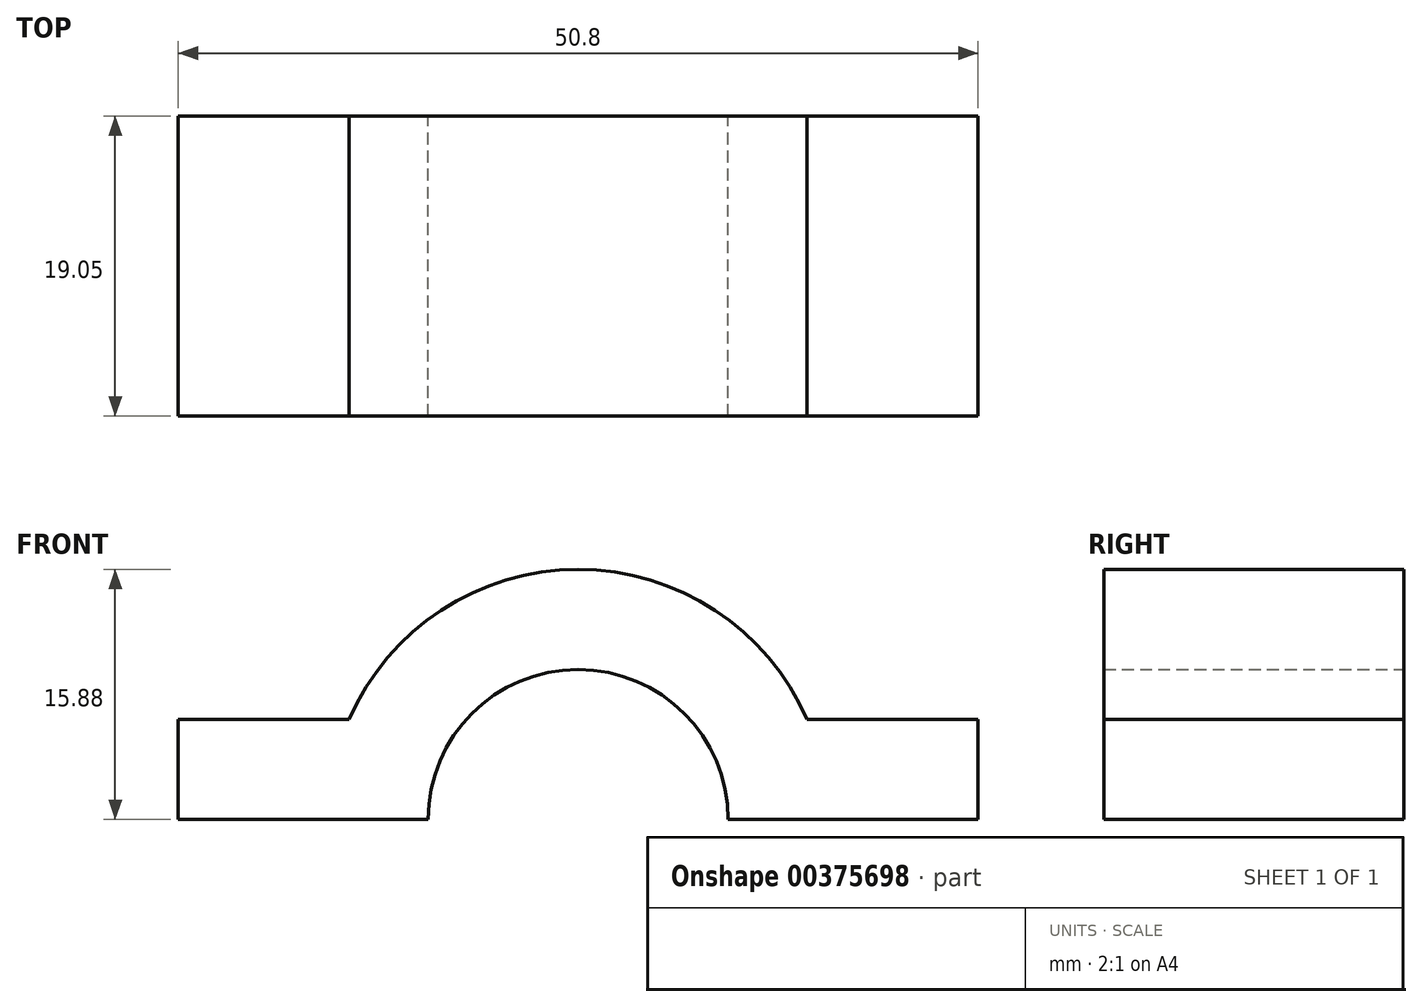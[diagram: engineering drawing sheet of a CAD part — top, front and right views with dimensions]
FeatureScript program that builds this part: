
annotation { "Feature Type Name" : "Feature", "Feature Type Description" : "" }
export const myFeature = defineFeature(function(context is Context, id is Id, definition is map)
    precondition{}
    {
        {
            var Q0;
            Q0=qCreatedBy(makeId("Front.planeOp"),FACE);
            var sketch = newSketch(context, id + "F0", { "sketchPlane" : qUnion([Q0])});
            skLineSegment(sketch, "E0.bottom", {"start": v(34.59, 3.77) * mm, "end": v(16.29, 3.77) * mm});
            skLineSegment(sketch, "E0.top", {"start": v(34.59, -2.58) * mm, "end": v(18.71, -2.58) * mm});
            skLineSegment(sketch, "E0.left", {"start": v(34.59, 3.77) * mm, "end": v(34.59, -2.58) * mm});
            skLineSegment(sketch, "E0.right", {"start": v(-16.21, 3.77) * mm, "end": v(-16.21, -2.58) * mm});
            skPoint(sketch, "E0.middle", {"position": v(9.19, 0.6) * mm});
            skPoint(sketch, "E1", {"position": v(9.19, 13.3) * mm});
            skPoint(sketch, "E2", {"position": v(-6.69, -2.58) * mm});
            skPoint(sketch, "E3", {"position": v(25.06, -2.58) * mm});
            skArc(sketch, "E4", {"start": v(25.06, -2.58) * mm, "mid": v(9.19, 13.3) * mm, "end": v(-6.69, -2.58) * mm});
            skPoint(sketch, "E5", {"position": v(18.71, -2.58) * mm});
            skPoint(sketch, "E6", {"position": v(-0.34, -2.58) * mm});
            skPoint(sketch, "E7", {"position": v(9.19, 6.95) * mm});
            skArc(sketch, "E8", {"start": v(18.71, -2.58) * mm, "mid": v(9.19, 6.95) * mm, "end": v(-0.34, -2.58) * mm});
            skLineSegment(sketch, "E9.trimOffspring", {"start": v(2.09, 3.77) * mm, "end": v(-16.21, 3.77) * mm});
            skLineSegment(sketch, "E10.trimOffspring", {"start": v(-0.34, -2.58) * mm, "end": v(-16.21, -2.58) * mm});
            skSolve(sketch);
        }
        {
            var Q0;
            Q0 = qSketchRegion(id + "F0", true);
            extrude(context, id + "F1", {"entities" : qUnion([Q0]), "depth" : 19.05 * mm});
        }
    });
